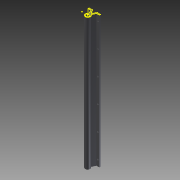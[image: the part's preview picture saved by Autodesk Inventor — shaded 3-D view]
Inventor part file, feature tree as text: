
AUTODESK INVENTOR PART (.ipt)
format: ipt  version: 2013 (Build 170138000, 138)  size: 158,720 bytes
history: native  units: in
note: dims shown in document units (in); Inventor stores cm internally (conversion verified against a paired STEP export)
features: sketch x2, imported_body x1
ambient origin geometry x8: Origin, YZ Plane, XZ Plane, XY Plane, X Axis, Y Axis, Z Axis, Center Point
feature tree (3):
  sketch  "Sketch4"
  sketch  "Sketch5"
  imported_body  "Base1"
